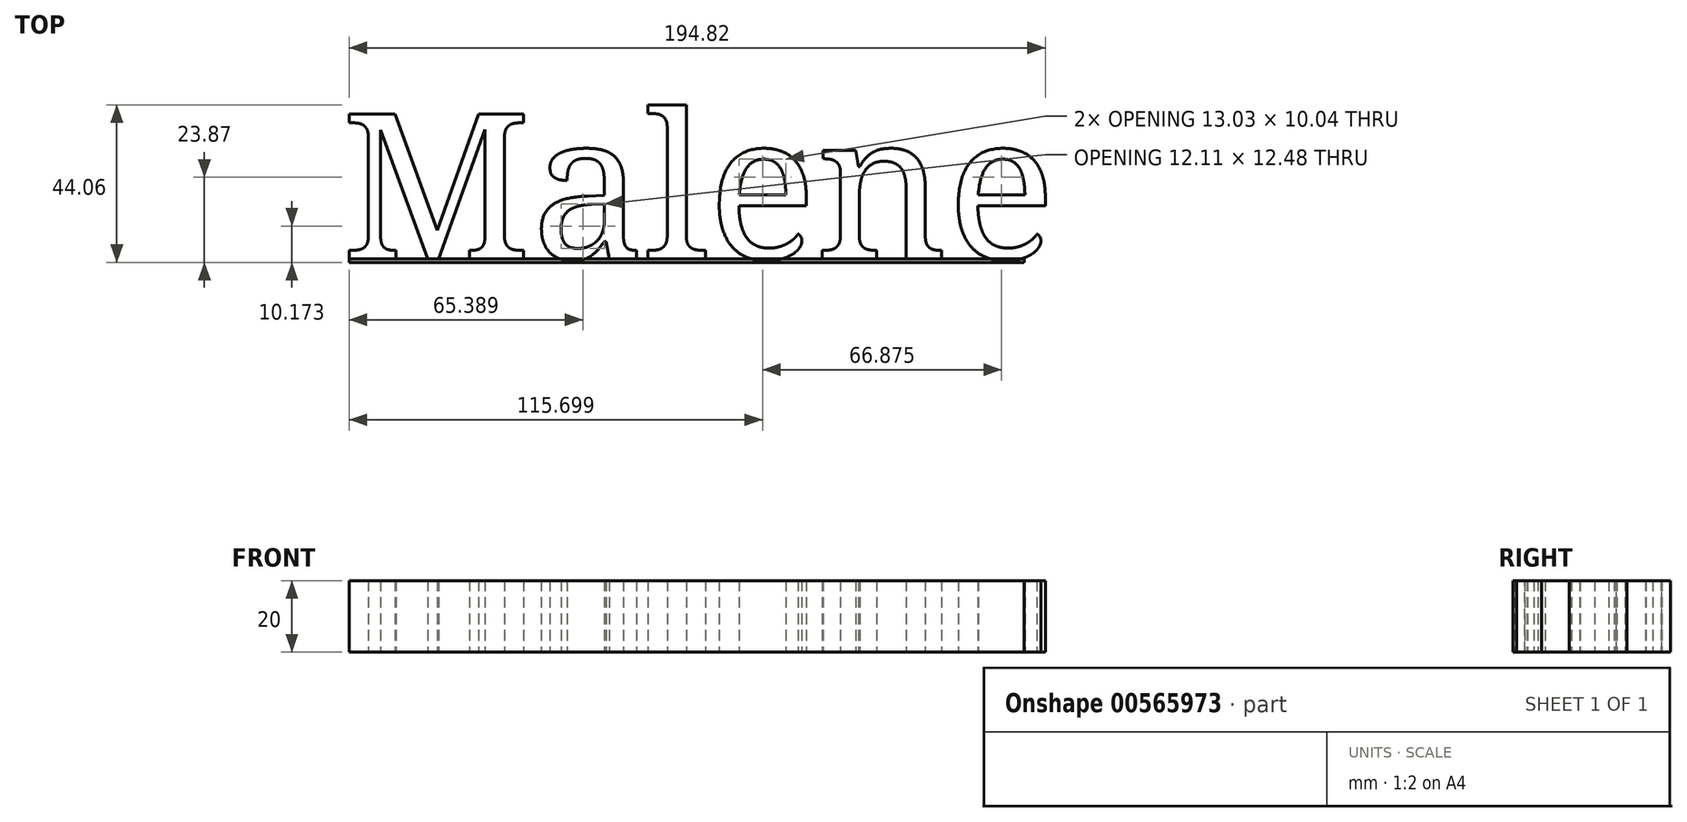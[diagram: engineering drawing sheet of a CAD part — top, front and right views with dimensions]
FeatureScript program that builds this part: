
annotation { "Feature Type Name" : "Feature", "Feature Type Description" : "" }
export const myFeature = defineFeature(function(context is Context, id is Id, definition is map)
    precondition{}
    {
        {
            var Q0;
            Q0=qCreatedBy(makeId("Top.planeOp"),FACE);
            var sketch = newSketch(context, id + "F0", { "sketchPlane" : qUnion([Q0])});
            skText(sketch, "E0", { "text": "Malene", "fontName": "NotoSerif-Regular.ttf"});
            const initialGuessF0  = {"E0": [-0.1101, -0.05228, 1, 0, 0.0408]};
            skSetInitialGuess(sketch, initialGuessF0);
            skSolve(sketch);
        }
        {
            var Q0;
            Q0 = qSketchRegion(id + "F0", true);
            extrude(context, id + "F1", {"entities" : qUnion([Q0]), "depth" : 20 * mm, "offsetDistance" : 25.4 * mm});
        }
        {
            var Q0;
            Q0=makeQuery(id+"F1.opExtrude","SWEPT_FACE",FACE,{"disambiguationData":[OSD([sQuery(id+"F0.wireOp",EDGE,"E0.sketch_text.stroke-17")])]});
            var sketch = newSketch(context, id + "F2", { "sketchPlane" : qUnion([Q0])});
            skLineSegment(sketch, "E1.bottom", {"start": v(-107.95, 20) * mm, "end": v(80.96, 20) * mm});
            skLineSegment(sketch, "E1.top", {"start": v(-107.95, 0) * mm, "end": v(80.96, 0) * mm});
            skLineSegment(sketch, "E1.left", {"start": v(-107.95, 20) * mm, "end": v(-107.95, 0) * mm});
            skLineSegment(sketch, "E1.right", {"start": v(80.96, 20) * mm, "end": v(80.96, 0) * mm});
            skSolve(sketch);
        }
        {
            var Q0;
            Q0 = qSketchRegion(id + "F2", true);
            extrude(context, id + "F3", {"entities" : qUnion([Q0]), "depth" : 1 * mm, "offsetDistance" : 25.4 * mm});
        }
    });
